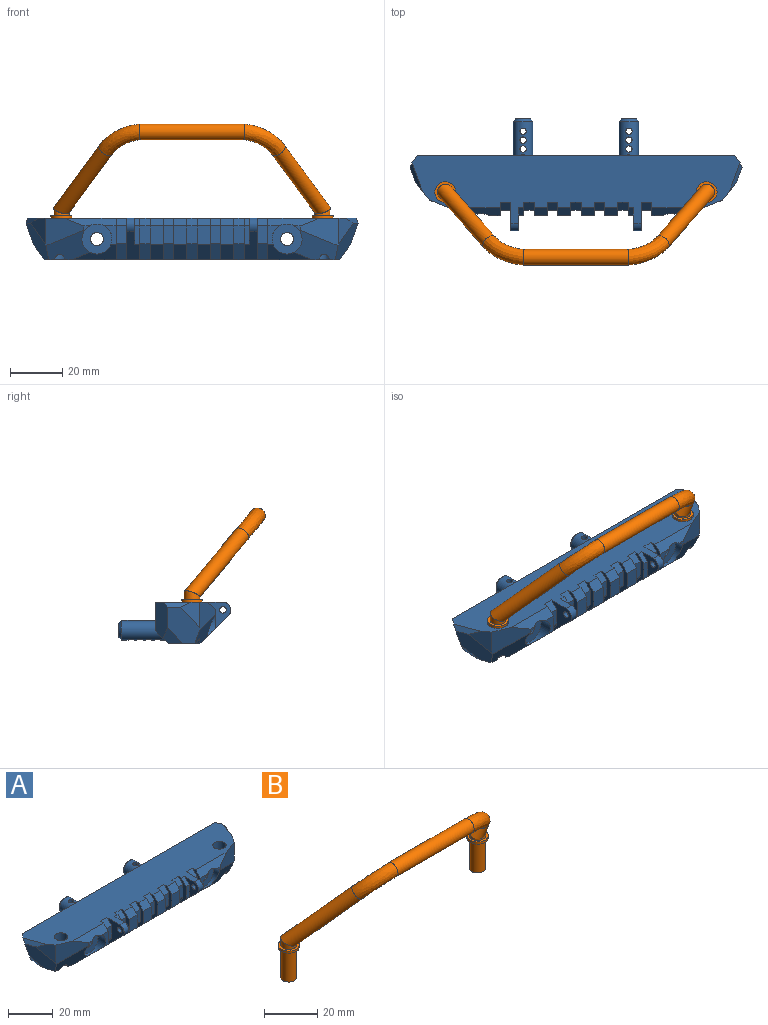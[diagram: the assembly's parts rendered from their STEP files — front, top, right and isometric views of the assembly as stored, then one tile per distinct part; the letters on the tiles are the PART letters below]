
ASSEMBLY  parts=2 mates=1
PART A: 130 faces, bbox 127.9x43.7x22.1 mm
  f0: plane 7x2mm, normal (0,-1,0), area 14mm2, adj f1,f15,f50,f129
  f1: plane 3x3mm, normal (0,-0.71,0.71), area 8.5mm2, adj f0,f22,f50,f129
  f2: plane 7x2mm, normal (0,-1,0), area 14mm2, adj f3,f20,f62,f128
  f3: plane 3x3mm, normal (0,-0.71,0.71), area 8.5mm2, adj f2,f22,f62,f128
  f4: plane 75x15mm, normal (0,0,-1), area 1072.2mm2, adj f5,f7,f8,f12,f13,f35,f111,f113
  f5: plane 17.25x14mm, normal (0,1,0), area 70.9mm2, adj f4,f23,f40,f112,f114,f127
  f6: cylinder r=5.5mm len=11mm, axis (0,-1,0), area 77.6mm2, adj f8,f10,f111,f124,f125
  f7: plane 40.5x14mm, normal (0,1,0), area 360.7mm2, adj f4,f23,f114,f116
  f8: plane 17.25x14mm, normal (0,1,0), area 70.9mm2, adj f4,f6,f10,f23,f116,f124
  f9: cylinder r=2.5mm len=7mm, axis (0,-1,0), area 110mm2, adj f69,f113
  f10: cylinder r=10mm len=13.02mm, axis (0,0,-1), area 158.7mm2, adj f6,f8,f12,f23,f119,f125
  f11: cylinder r=2.5mm len=7mm, axis (0,-1,0), area 110mm2, adj f68,f111
  f12: plane 15.47x14.19mm, normal (-0.2,0,-0.98), area 125.9mm2, adj f4,f10,f35,f111,f119,f125
  f13: plane 15.47x14.19mm, normal (0.2,0,-0.98), area 125.9mm2, adj f4,f35,f40,f113,f118,f126
  f14: cylinder r=3mm len=16mm, axis (0,0,1), area 294.3mm2, adj f22,f23,f34
  f15: plane 10.95x10.95mm, normal (0,-0.71,-0.71), area 63.4mm2, adj f0,f23,f48,f50,f87,f129
  f16: plane 6x6mm, normal (0,-0.71,-0.71), area 42.4mm2, adj f23,f32,f51,f53
  f17: plane 6x6mm, normal (0,-0.71,-0.71), area 42.4mm2, adj f23,f31,f54,f57
  f18: plane 6x6mm, normal (0,-0.71,-0.71), area 42.4mm2, adj f23,f30,f56,f60
  f19: plane 6x6mm, normal (0,-0.71,-0.71), area 42.4mm2, adj f23,f29,f59,f63
  f20: plane 10.95x10.95mm, normal (0,-0.71,-0.71), area 63.4mm2, adj f2,f23,f62,f66,f85,f128
  f21: plane 17.15x6mm, normal (0,-0.71,-0.71), area 65.6mm2, adj f23,f25,f34,f45,f65
  f22: plane 125.52x26mm, normal (0,0,1), area 2287.4mm2, adj f1,f3,f14,f35,f36,f37,f38,f39
  f23: plane 113.84x12.84mm, normal (0,0,-1), area 362.5mm2, adj f5,f7,f8,f10,f14,f15,f16,f17
  f24: plane 2.19x1.79mm, normal (0,-1,0), area 1.9mm2, adj f27,f39,f46,f78
  f25: plane 7x4.54mm, normal (0,-1,0), area 15.8mm2, adj f21,f45,f65,f77
  f26: plane 17.15x6mm, normal (0,-0.71,-0.71), area 65.6mm2, adj f23,f27,f33,f46,f47
  f27: plane 16.9x11.34mm, normal (0.21,-0.9,-0.39), area 120.6mm2, adj f23,f24,f26,f39,f43,f46,f89
  f28: plane 2.19x1.79mm, normal (0,-1,0), area 1.9mm2, adj f34,f38,f45,f77
  f29: plane 7x5mm, normal (0,-1,0), area 35mm2, adj f19,f59,f63,f82
  f30: plane 7x5mm, normal (0,-1,0), area 35mm2, adj f18,f56,f60,f81
  f31: plane 7x5mm, normal (0,-1,0), area 35mm2, adj f17,f54,f57,f80
  f32: plane 7x5mm, normal (0,-1,0), area 35mm2, adj f16,f51,f53,f79
  f33: plane 7x4.54mm, normal (0,-1,0), area 15.8mm2, adj f26,f46,f47,f78
  f34: plane 16.9x11.34mm, normal (-0.21,-0.9,-0.39), area 120.6mm2, adj f14,f21,f23,f28,f38,f44,f45
  f35: plane 121.28x11mm, normal (0,1,0), area 391.8mm2, adj f4,f12,f13,f22,f118,f119,f120,f121
  f36: plane 9.81x7.23mm, normal (0.8,-0.6,0), area 48.4mm2, adj f22,f39,f43,f83
  f37: plane 9.81x7.23mm, normal (-0.8,-0.6,0), area 48.4mm2, adj f22,f38,f44,f84
  f38: plane 14.81x10.54mm, normal (-0.38,-0.93,0), area 110.3mm2, adj f22,f28,f34,f37,f44,f77
  f39: plane 14.81x10.54mm, normal (0.38,-0.93,0), area 110.3mm2, adj f22,f24,f27,f36,f43,f78
  f40: cylinder r=10mm len=13.02mm, axis (0,0,-1), area 158.7mm2, adj f5,f13,f23,f112,f118,f126
  f41: plane 7.51x6.21mm, normal (-0.82,0,-0.57), area 27.9mm2, adj f23,f44,f120,f123
  f42: plane 7.51x6.21mm, normal (0.82,0,-0.57), area 27.9mm2, adj f23,f43,f121,f122
  f43: plane 14.1x12.4mm, normal (0.89,-0.33,-0.31), area 136.8mm2, adj f23,f27,f36,f39,f42,f83,f122
  f44: plane 14.1x12.4mm, normal (-0.89,-0.33,-0.31), area 136.8mm2, adj f23,f34,f37,f38,f41,f84,f123
  f45: cylinder r=5.75mm len=11.5mm, axis (0,-1,0), area 131.9mm2, adj f21,f25,f28,f34,f69,f77
  f46: cylinder r=5.75mm len=11.5mm, axis (0,-1,0), area 131.9mm2, adj f24,f26,f27,f33,f68,f78
  f47: plane 16x6.14mm, normal (-1,0,0), area 26.8mm2, adj f22,f23,f26,f33,f49,f70,f78,f90
  f48: plane 16x11.95mm, normal (1,0,0), area 65.6mm2, adj f15,f22,f23,f49,f70,f87,f88,f90
  f49: plane 6.81x4mm, normal (0,-1,0), area 27.2mm2, adj f47,f48,f70,f90
  f50: plane 16x6.14mm, normal (-1,0,0), area 26.8mm2, adj f0,f1,f15,f22,f23,f52,f71,f91
  f51: plane 16x6.14mm, normal (1,0,0), area 26.8mm2, adj f16,f22,f23,f32,f52,f71,f79,f91
  f52: plane 6.81x4mm, normal (0,-1,0), area 27.2mm2, adj f50,f51,f71,f91
  f53: plane 16x6.14mm, normal (-1,0,0), area 26.8mm2, adj f16,f22,f23,f32,f55,f72,f79,f92
  f54: plane 16x6.14mm, normal (1,0,0), area 26.8mm2, adj f17,f22,f23,f31,f55,f72,f80,f92
  f55: plane 6.81x4mm, normal (0,-1,0), area 27.2mm2, adj f53,f54,f72,f92
  f56: plane 16x6.14mm, normal (1,0,0), area 26.8mm2, adj f18,f22,f23,f30,f58,f73,f81,f93
  f57: plane 16x6.14mm, normal (-1,0,0), area 26.8mm2, adj f17,f22,f23,f31,f58,f73,f80,f93
  f58: plane 6.81x4mm, normal (0,-1,0), area 27.2mm2, adj f56,f57,f73,f93
  f59: plane 16x6.14mm, normal (1,0,0), area 26.8mm2, adj f19,f22,f23,f29,f61,f74,f82,f94
  f60: plane 16x6.14mm, normal (-1,0,0), area 26.8mm2, adj f18,f22,f23,f30,f61,f74,f81,f94
  f61: plane 6.81x4mm, normal (0,-1,0), area 27.2mm2, adj f59,f60,f74,f94
  f62: plane 16x6.14mm, normal (1,0,0), area 26.8mm2, adj f2,f3,f20,f22,f23,f64,f75,f95
  f63: plane 16x6.14mm, normal (-1,0,0), area 26.8mm2, adj f19,f22,f23,f29,f64,f75,f82,f95
  f64: plane 6.81x4mm, normal (0,-1,0), area 27.2mm2, adj f62,f63,f75,f95
  f65: plane 16x6.14mm, normal (1,0,0), area 26.8mm2, adj f21,f22,f23,f25,f67,f76,f77,f96
  f66: plane 16x11.95mm, normal (-1,0,0), area 65.6mm2, adj f20,f22,f23,f67,f76,f85,f86,f96
  f67: plane 6.81x4mm, normal (0,-1,0), area 27.2mm2, adj f65,f66,f76,f96
  f68: plane 11.5x11.5mm, normal (0,-1,0), area 84.2mm2, adj f11,f46
  f69: plane 11.5x11.5mm, normal (0,-1,0), area 84.2mm2, adj f9,f45
  f70: plane 4x3mm, normal (0,-0.71,0.71), area 17mm2, adj f22,f47,f48,f49
  f71: plane 4x3mm, normal (0,-0.71,0.71), area 17mm2, adj f22,f50,f51,f52
  f72: plane 4x3mm, normal (0,-0.71,0.71), area 17mm2, adj f22,f53,f54,f55
  f73: plane 4x3mm, normal (0,-0.71,0.71), area 17mm2, adj f22,f56,f57,f58
  f74: plane 4x3mm, normal (0,-0.71,0.71), area 17mm2, adj f22,f59,f60,f61
  f75: plane 4x3mm, normal (0,-0.71,0.71), area 17mm2, adj f22,f62,f63,f64
  f76: plane 4x3mm, normal (0,-0.71,0.71), area 17mm2, adj f22,f65,f66,f67
  f77: plane 19.81x3mm, normal (0,-0.71,0.71), area 64.3mm2, adj f22,f25,f28,f38,f45,f65
  f78: plane 19.81x3mm, normal (0,-0.71,0.71), area 64.3mm2, adj f22,f24,f33,f39,f46,f47
  f79: plane 5x3mm, normal (0,-0.71,0.71), area 21.2mm2, adj f22,f32,f51,f53
  f80: plane 5x3mm, normal (0,-0.71,0.71), area 21.2mm2, adj f22,f31,f54,f57
  f81: plane 5x3mm, normal (0,-0.71,0.71), area 21.2mm2, adj f22,f30,f56,f60
  f82: plane 5x3mm, normal (0,-0.71,0.71), area 21.2mm2, adj f22,f29,f59,f63
  f83: plane 10.8x4.77mm, normal (0.76,-0.28,0.59), area 19.8mm2, adj f22,f36,f43,f122
  f84: plane 10.8x4.77mm, normal (-0.76,-0.28,0.59), area 19.8mm2, adj f22,f37,f44,f123
  f85: cylinder r=2.96mm len=5.05mm, axis (-1,0,0), area 20.5mm2, adj f20,f22,f66,f128
  f86: cylinder r=1.25mm len=3mm, axis (-1,0,0), area 23.6mm2, adj f66,f128
  f87: cylinder r=2.96mm len=5.05mm, axis (1,0,0), area 20.5mm2, adj f15,f22,f48,f129
  f88: cylinder r=1.25mm len=3mm, axis (1,0,0), area 23.6mm2, adj f48,f129
  f89: cylinder r=3mm len=16mm, axis (0,0,1), area 294.3mm2, adj f22,f23,f27
  f90: plane 6.19x4.14mm, normal (0,-0.83,-0.56), area 29.8mm2, adj f23,f47,f48,f49
  f91: plane 6.19x4.14mm, normal (0,-0.83,-0.56), area 29.8mm2, adj f23,f50,f51,f52
  f92: plane 6.19x4.14mm, normal (0,-0.83,-0.56), area 29.8mm2, adj f23,f53,f54,f55
  f93: plane 6.19x4.14mm, normal (0,-0.83,-0.56), area 29.8mm2, adj f23,f56,f57,f58
  f94: plane 6.19x4.14mm, normal (0,-0.83,-0.56), area 29.8mm2, adj f23,f59,f60,f61
  f95: plane 6.19x4.14mm, normal (0,-0.83,-0.56), area 29.8mm2, adj f23,f62,f63,f64
  f96: plane 6.19x4.14mm, normal (0,-0.83,-0.56), area 29.8mm2, adj f23,f65,f66,f67
  f97: plane 5.5x5.5mm, normal (0,1,0), area 23.8mm2, adj f102
  f98: cylinder r=1.2mm len=7.3mm, axis (0,0,-1), area 54.3mm2, adj f103
  f99: cylinder r=1.2mm len=7.3mm, axis (0,0,-1), area 54.3mm2, adj f103
  f100: cylinder r=1.2mm len=7.3mm, axis (0,0,-1), area 54.3mm2, adj f103
  f101: cylinder r=1.2mm len=7.3mm, axis (0,0,-1), area 54.3mm2, adj f103
  f102: cone r=3.75mm half-angle=45deg, axis (0,-1,0), area 28.9mm2, adj f97,f103
  f103: cylinder r=3.75mm len=24.43mm, axis (0,-1,0), area 511.9mm2, adj f98,f99,f100,f101,f102,f114,f115
  f104: plane 5.5x5.5mm, normal (0,1,0), area 23.8mm2, adj f109
  f105: cylinder r=1.2mm len=7.3mm, axis (0,0,-1), area 54.3mm2, adj f110
  f106: cylinder r=1.2mm len=7.3mm, axis (0,0,-1), area 54.3mm2, adj f110
  f107: cylinder r=1.2mm len=7.3mm, axis (0,0,-1), area 54.3mm2, adj f110
  f108: cylinder r=1.2mm len=7.3mm, axis (0,0,-1), area 54.3mm2, adj f110
  f109: cone r=2.75mm half-angle=45deg, axis (0,-1,0), area 28.9mm2, adj f104,f110
  f110: cylinder r=3.75mm len=24.43mm, axis (0,-1,0), area 511.9mm2, adj f105,f106,f107,f108,f109,f116,f117
  f111: plane 11.53x11.5mm, normal (0,1,0), area 89.5mm2, adj f4,f6,f11,f12,f124,f125
  f112: cylinder r=5.5mm len=11mm, axis (0,-1,0), area 77.6mm2, adj f5,f40,f113,f126,f127
  f113: plane 11.53x11.5mm, normal (0,1,0), area 89.5mm2, adj f4,f9,f13,f112,f126,f127
  f114: torus R=8.75mm, axis (0,1,0), area 193.6mm2, adj f5,f7,f103,f115
  f115: bspline ~14.53x5.29mm, area 46.2mm2, adj f23,f103,f114
  f116: torus R=8.75mm, axis (0,1,0), area 193.6mm2, adj f7,f8,f110,f117
  f117: bspline ~14.53x5.29mm, area 46.2mm2, adj f23,f110,f116
  f118: plane 12x5mm, normal (0.71,0.71,0), area 63.6mm2, adj f13,f35,f40,f120
  f119: plane 12x5mm, normal (-0.71,0.71,0), area 63.6mm2, adj f10,f12,f35,f121
  f120: plane 10.46x5mm, normal (0,0.71,-0.71), area 51.7mm2, adj f23,f35,f41,f118,f123
  f121: plane 10.46x5mm, normal (0,0.71,-0.71), area 51.7mm2, adj f23,f35,f42,f119,f122
  f122: plane 13.88x6.72mm, normal (0.77,0.58,-0.27), area 72.5mm2, adj f22,f35,f42,f43,f83,f121
  f123: plane 13.88x6.72mm, normal (-0.77,0.58,-0.27), area 72.5mm2, adj f22,f35,f41,f44,f84,f120
  f124: cylinder r=5mm len=4.11mm, axis (0,-1,0), area 17mm2, adj f4,f6,f8,f111
  f125: cylinder r=5mm len=3.8mm, axis (0,1,0), area 11.4mm2, adj f6,f10,f12,f111
  f126: cylinder r=5mm len=3.8mm, axis (0,-1,0), area 11.4mm2, adj f13,f40,f112,f113
  f127: cylinder r=5mm len=4.11mm, axis (0,1,0), area 17mm2, adj f4,f5,f112,f113
  f128: plane 10x8.82mm, normal (1,0,0), area 38.8mm2, adj f2,f3,f20,f22,f85,f86
  f129: plane 10x8.82mm, normal (-1,0,0), area 38.8mm2, adj f0,f1,f15,f22,f87,f88
PART B: 17 faces, bbox 108x32x50 mm
  f0: cylinder r=3mm len=40mm, axis (1,0,0), area 751.9mm2, adj f2,f5
  f1: cylinder r=3mm len=28.51mm, axis (0.49,-0.56,0.67), area 656.6mm2, adj f2,f3
  f2: bspline ~16.05x12.02mm, area 306.9mm2, adj f0,f1
  f3: cylinder r=3mm len=6mm, axis (0,0,1), area 36.3mm2, adj f1,f9
  f4: cylinder r=3mm len=28.51mm, axis (-0.49,-0.56,0.67), area 656.6mm2, adj f5,f6
  f5: bspline ~16.05x12.02mm, area 306.9mm2, adj f0,f4
  f6: cylinder r=3mm len=6mm, axis (0,0,1), area 36.3mm2, adj f4,f12
  f7: cylinder r=4mm len=8mm, axis (0,0,1), area 25.1mm2, adj f8,f9
  f8: plane 8x8mm, normal (0,0,-1), area 23.8mm2, adj f7,f13
  f9: plane 8x8mm, normal (0,0,1), area 22mm2, adj f3,f7
  f10: cylinder r=4mm len=8mm, axis (0,0,1), area 25.1mm2, adj f11,f12
  f11: plane 8x8mm, normal (0,0,-1), area 23.8mm2, adj f10,f15
  f12: plane 8x8mm, normal (0,0,1), area 22mm2, adj f6,f10
  f13: cylinder r=2.9mm len=14mm, axis (0,0,1), area 255.1mm2, adj f8,f14
  f14: plane 5.8x5.8mm, normal (0,0,-1), area 26.4mm2, adj f13
  f15: cylinder r=2.9mm len=14mm, axis (0,0,1), area 255.1mm2, adj f11,f16
  f16: plane 5.8x5.8mm, normal (0,0,-1), area 26.4mm2, adj f15
PLACE A at identity
PLACE B t=(0,-2.52,5)mm
MATE fastened B.f10 <-> A.f89  axis (0,0,-1) through (50,-2.52,16)mm
